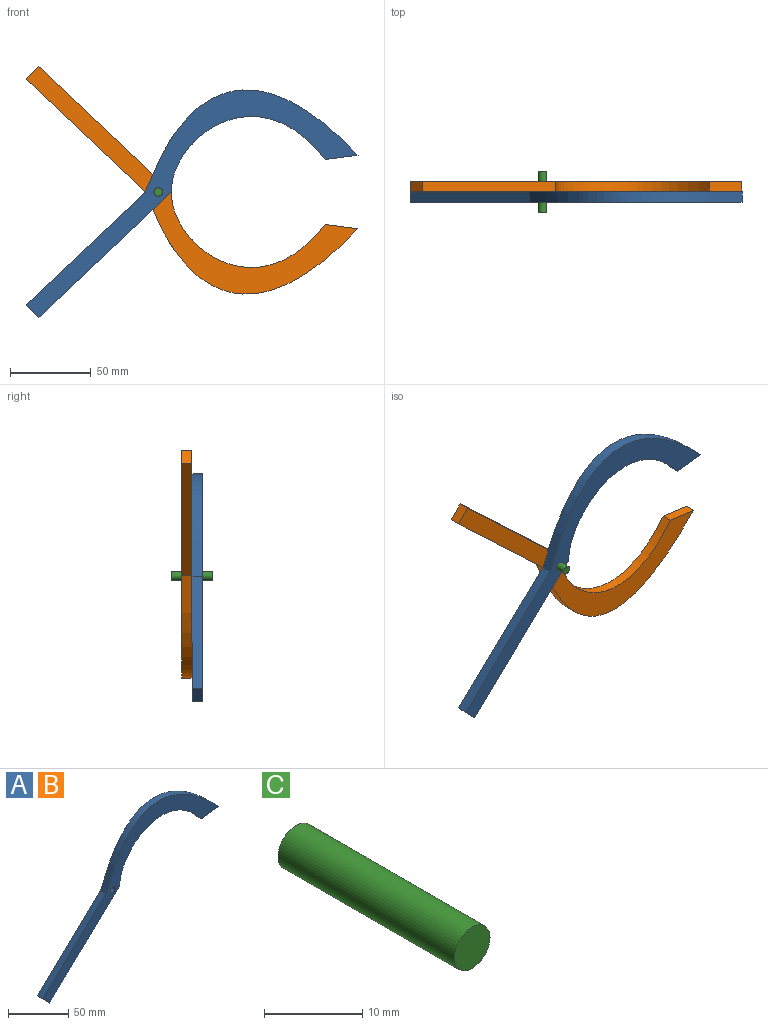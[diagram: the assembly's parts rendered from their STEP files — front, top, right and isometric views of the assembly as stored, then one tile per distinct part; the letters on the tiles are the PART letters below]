
ASSEMBLY  parts=3 mates=2
PART A: 9 faces, bbox 205.7x6.4x161.4 mm
  f0: extruded ~131.86x63.23mm, area 1124.4mm2, adj f1,f5,f7,f8
  f1: plane 73.79x69.84mm, normal (-0.69,0,0.73), area 645.2mm2, adj f0,f2,f7,f8
  f2: plane 8.14x7.71mm, normal (-0.73,0,-0.69), area 71.2mm2, adj f1,f3,f7,f8
  f3: plane 82.39x77.99mm, normal (0.69,0,-0.73), area 720.4mm2, adj f2,f4,f7,f8
  f4: extruded ~95.33x46.74mm, area 823.7mm2, adj f3,f5,f7,f8
  f5: plane 20.22x6.35mm, normal (0.13,0,-0.99), area 129.4mm2, adj f0,f4,f7,f8
  f6: cylinder r=2.75mm len=6.35mm, axis (0,1,0), area 109.7mm2, adj f7,f8
  f7: plane 205.65x161.35mm, normal (0,-1,0), area 3408.3mm2, adj f0,f1,f2,f3,f4,f5,f6
  f8: plane 205.65x161.35mm, normal (0,1,0), area 3408.3mm2, adj f0,f1,f2,f3,f4,f5,f6
PART B: same geometry as A
PART C: 3 faces, bbox 5.2x25.4x5.2 mm
  f0: cylinder r=2.58mm len=25.4mm, axis (0,1,0), area 411.4mm2, adj f1,f2
  f1: plane 5.16x5.16mm, normal (0,-1,0), area 20.9mm2, adj f0
  f2: plane 5.16x5.16mm, normal (0,1,0), area 20.9mm2, adj f0
PLACE A t=(-50.69,-11.5,29.39)mm
PLACE B rot(axis=(1,0,0),180deg) t=(-50.69,-11.5,29.39)mm
PLACE C t=(-82.64,1.2,29.39)mm
MATE revolute A.f6 <-> C.f0  axis (0,1,0) through (-82.64,-11.5,29.39)mm
MATE revolute C.f0 <-> B.f6  axis (0,1,0) through (-82.64,-11.5,29.39)mm
